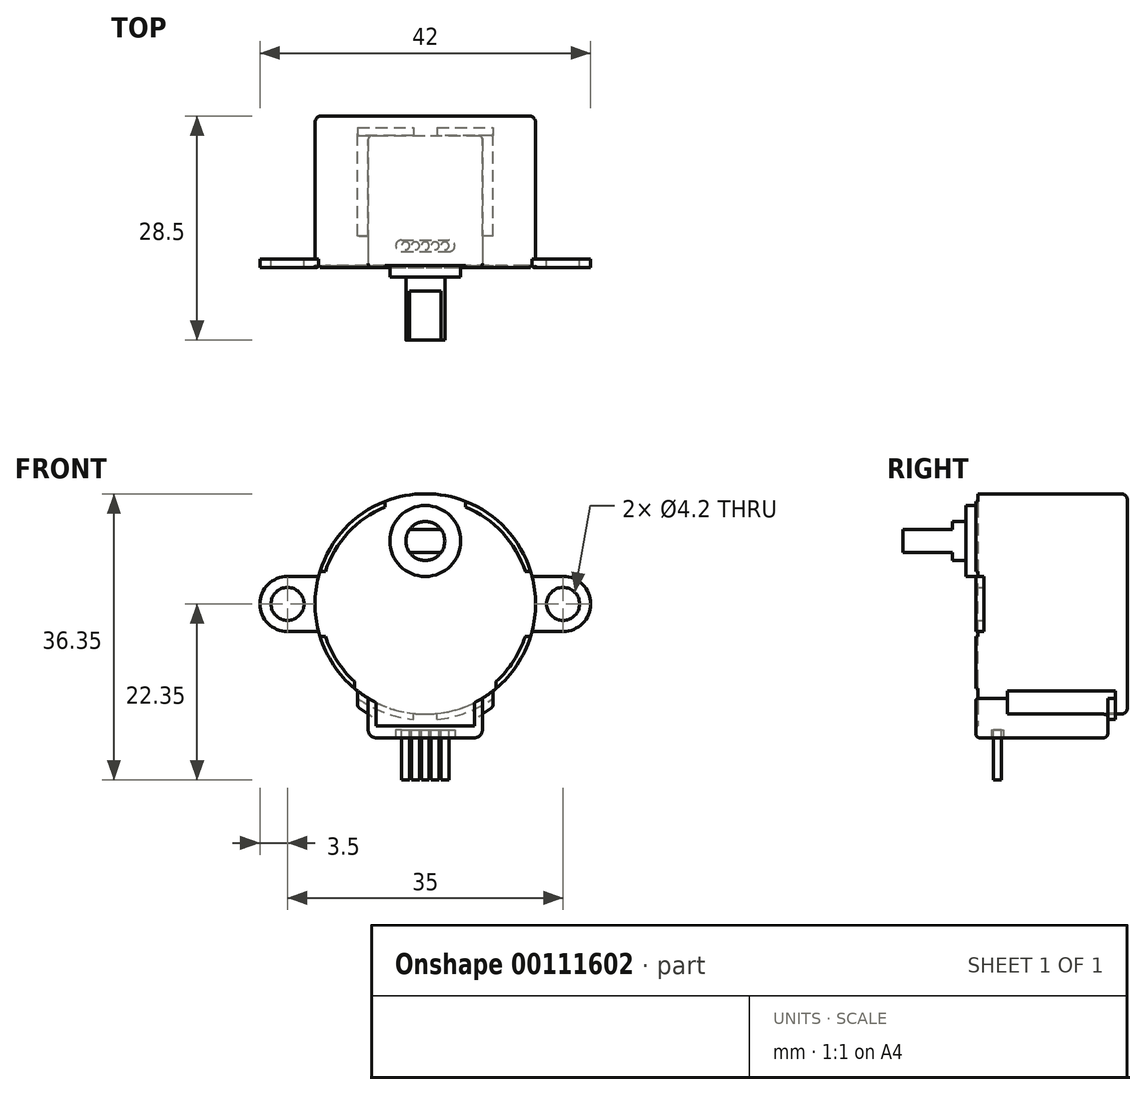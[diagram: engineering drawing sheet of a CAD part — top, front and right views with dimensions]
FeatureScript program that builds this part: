
annotation { "Feature Type Name" : "Feature", "Feature Type Description" : "" }
export const myFeature = defineFeature(function(context is Context, id is Id, definition is map)
    precondition{}
    {
        {
            var Q0;
            Q0=qCreatedBy(makeId("Front.planeOp"),FACE);
            var sketch = newSketch(context, id + "F0", { "sketchPlane" : qUnion([Q0])});
            skCircle(sketch, "E0", {"center": v(0, 0) * mm, "radius": 14 * mm});
            skSolve(sketch);
        }
        {
            var Q0;
            Q0=makeQuery(id+"F0.imprint","IMPRINT",FACE,{"disambiguationData":[TD([[makeQuery(id+"F0.imprint","IMPRINT",EDGE,{"derivedFrom":sQuery(id+"F0.wireOp",EDGE,"E0")}),1.0]])]});
            extrude(context, id + "F1", {"entities" : qUnion([Q0]), "depth" : 19 * mm});
        }
        {
            var Q0;
            Q0=makeQuery(id+"F1.opExtrude","CAP_EDGE",EDGE,{"disambiguationData":[OSD([sQuery(id+"F0.wireOp",EDGE,"E0")])],"isStart":true});
            fillet(context, id + "F2", {"entities" : qUnion([Q0]), "radius" : 0.8 * mm, "tangentPropagation" : true, "allowEdgeOverflow" : false});
        }
        {
            var Q0;
            Q0=makeQuery(id+"F1.opExtrude","CAP_FACE",FACE,{"disambiguationData":[OSD([sQuery(id+"F0.wireOp",EDGE,"E0")])],"isStart":false});
            var sketch = newSketch(context, id + "F3", { "sketchPlane" : qUnion([Q0])});
            skArc(sketch, "E1", {"start": v(12.7, 4.12) * mm, "mid": v(9.8, 9.06) * mm, "end": v(5.12, 12.33) * mm});
            skArc(sketch, "E2", {"start": v(-5.12, 12.33) * mm, "mid": v(-9.8, 9.06) * mm, "end": v(-12.7, 4.13) * mm});
            skLineSegment(sketch, "E3", {"start": v(-5.12, 12.33) * mm, "end": v(-5.12, 13.03) * mm});
            skLineSegment(sketch, "E4", {"start": v(-12.7, 4.12) * mm, "end": v(-13.38, 4.12) * mm});
            skLineSegment(sketch, "E5", {"start": v(12.7, 4.12) * mm, "end": v(13.38, 4.12) * mm});
            skLineSegment(sketch, "E6", {"start": v(5.12, 12.33) * mm, "end": v(5.12, 13.03) * mm});
            skArc(sketch, "E7", {"start": v(-12.7, -4.13) * mm, "mid": v(-11.22, -7.23) * mm, "end": v(-9, -9.86) * mm});
            skArc(sketch, "E8", {"start": v(9, -9.86) * mm, "mid": v(11.22, -7.23) * mm, "end": v(12.7, -4.12) * mm});
            skLineSegment(sketch, "E9", {"start": v(12.7, -4.12) * mm, "end": v(13.38, -4.12) * mm});
            skLineSegment(sketch, "E10", {"start": v(-12.7, -4.13) * mm, "end": v(-13.38, -4.13) * mm});
            skLineSegment(sketch, "E11", {"start": v(-9, -9.86) * mm, "end": v(-9, -10.72) * mm});
            skLineSegment(sketch, "E12", {"start": v(9, -9.86) * mm, "end": v(9, -10.72) * mm});
            skLineSegment(sketch, "E13", {"start": v(13.56, 3.5) * mm, "end": v(17.5, 3.5) * mm});
            skLineSegment(sketch, "E14", {"start": v(13.56, -3.5) * mm, "end": v(17.5, -3.5) * mm});
            skLineSegment(sketch, "E15", {"start": v(-13.56, 3.5) * mm, "end": v(-17.5, 3.5) * mm});
            skLineSegment(sketch, "E16", {"start": v(-13.56, -3.5) * mm, "end": v(-17.5, -3.5) * mm});
            skArc(sketch, "E17", {"start": v(17.5, -3.5) * mm, "mid": v(21, 0) * mm, "end": v(17.5, 3.5) * mm});
            skArc(sketch, "E18", {"start": v(-17.5, 3.5) * mm, "mid": v(-21, 0) * mm, "end": v(-17.5, -3.5) * mm});
            skCircle(sketch, "E19", {"center": v(-17.5, 0) * mm, "radius": 2.1 * mm});
            skCircle(sketch, "E20", {"center": v(17.5, 0) * mm, "radius": 2.1 * mm});
            skCircle(sketch, "E21", {"center": v(0, 8) * mm, "radius": 4.5 * mm});
            skSolve(sketch);
        }
        {
            var Q0;
            {var subQ1=sQuery(id+"F3.wireOp",EDGE,"E15");Q0=makeQuery(id+"F3.imprint","IMPRINT",FACE,{"disambiguationData":[TD([[makeQuery(id+"F3.imprint","IMPRINT",EDGE,{"derivedFrom":subQ1}),1.0]])]});}
            var Q1;
            {var subQ1=sQuery(id+"F3.wireOp",EDGE,"E13");Q1=makeQuery(id+"F3.imprint","IMPRINT",FACE,{"disambiguationData":[TD([[makeQuery(id+"F3.imprint","IMPRINT",EDGE,{"derivedFrom":subQ1}),-1.0]])]});}
            var Q2;
            Q2=makeQuery(id+"F3.imprint","IMPRINT",FACE,{"disambiguationData":[TD([[makeQuery(id+"F3.imprint","IMPRINT",EDGE,{"derivedFrom":sQuery(id+"F3.wireOp",EDGE,"E7")}),-1.0]])]});
            var Q3;
            Q3=makeQuery(id+"F3.imprint","IMPRINT",FACE,{"disambiguationData":[TD([[makeQuery(id+"F3.imprint","IMPRINT",EDGE,{"derivedFrom":sQuery(id+"F3.wireOp",EDGE,"E8")}),-1.0]])]});
            var Q4;
            Q4=makeQuery(id+"F3.imprint","IMPRINT",FACE,{"disambiguationData":[TD([[makeQuery(id+"F3.imprint","IMPRINT",EDGE,{"derivedFrom":sQuery(id+"F3.wireOp",EDGE,"E1")}),-1.0]])]});
            var Q5;
            Q5=makeQuery(id+"F3.imprint","IMPRINT",FACE,{"disambiguationData":[TD([[makeQuery(id+"F3.imprint","IMPRINT",EDGE,{"derivedFrom":sQuery(id+"F3.wireOp",EDGE,"E2")}),-1.0]])]});
            var Q6;
            Q6=makeQuery(id+"F3.imprint","IMPRINT",FACE,{"disambiguationData":[TD([[makeQuery(id+"F3.imprint","IMPRINT",EDGE,{"derivedFrom":sQuery(id+"F3.wireOp",EDGE,"E21")}),1.0]])]});
            extrude(context, id + "F4", {"entities" : qUnion([Q0, Q1, Q2, Q3, Q4, Q5, Q6]), "operationType" : NewBodyOperationType.ADD, "depth" : .25 * mm, "hasSecondDirection" : true, "secondDirectionOppositeDirection" : true, "secondDirectionDepth" : .8 * mm});
        }
        {
            var Q0;
            {var subQ0=sQuery(id+"F0.wireOp",EDGE,"E0");var subQ1=makeQuery(id+"F1.opExtrude","CAP_EDGE",EDGE,{"disambiguationData":[OSD([subQ0])],"isStart":false});Q0=makeQuery(id+"F4.opExtrude","CAP_EDGE",EDGE,{"disambiguationData":[OSD([subQ0]),TDD([makeQuery(id+"F3.imprint","IMPRINT",EDGE,{"disambiguationData":[TD([[makeQuery(id+"F3.imprint","INTERSECT",VERTEX,{"derivedFrom":[subQ1,sQuery(id+"F3.wireOp",EDGE,"E15")]}),-1.0]])],"derivedFrom":subQ1})])],"isStart":false});}
            var Q1;
            {var subQ0=sQuery(id+"F0.wireOp",EDGE,"E0");var subQ1=makeQuery(id+"F1.opExtrude","CAP_EDGE",EDGE,{"disambiguationData":[OSD([subQ0])],"isStart":false});Q1=makeQuery(id+"F4.opExtrude","CAP_EDGE",EDGE,{"disambiguationData":[OSD([subQ0]),TDD([makeQuery(id+"F3.imprint","IMPRINT",EDGE,{"disambiguationData":[TD([[makeQuery(id+"F3.imprint","INTERSECT",VERTEX,{"derivedFrom":[subQ1,sQuery(id+"F3.wireOp",EDGE,"E13")]}),1.0]])],"derivedFrom":subQ1})])],"isStart":false});}
            fillet(context, id + "F5", {"entities" : qUnion([Q0, Q1]), "radius" : 0.25 * mm, "tangentPropagation" : true, "allowEdgeOverflow" : false});
        }
        {
            var Q0;
            Q0=makeQuery(id+"F4.opExtrude","CAP_FACE",FACE,{"disambiguationData":[OSD([sQuery(id+"F3.wireOp",EDGE,"E21")])],"isStart":false});
            extrude(context, id + "F6", {"entities" : qUnion([Q0]), "operationType" : NewBodyOperationType.ADD, "depth" : 1.25 * mm});
        }
        {
            var Q0;
            Q0=makeQuery(id+"F1.opExtrude","CAP_FACE",FACE,{"disambiguationData":[OSD([sQuery(id+"F0.wireOp",EDGE,"E0")])],"isStart":false});
            var sketch = newSketch(context, id + "F7", { "sketchPlane" : qUnion([Q0])});
            skLineSegment(sketch, "E22", {"start": v(-7.25, -11.98) * mm, "end": v(-7.25, -16) * mm});
            skLineSegment(sketch, "E23", {"start": v(-6.25, -17) * mm, "end": v(6.25, -17) * mm});
            skLineSegment(sketch, "E24", {"start": v(7.25, -16) * mm, "end": v(7.25, -11.98) * mm});
            skPoint(sketch, "E25.visualSharp", {"position": v(-7.25, -17) * mm});
            skArc(sketch, "E25.filletArc", {"start": v(-7.25, -16) * mm, "mid": v(-6.96, -16.7) * mm, "end": v(-6.25, -17) * mm});
            skPoint(sketch, "E26.visualSharp", {"position": v(7.25, -17) * mm});
            skArc(sketch, "E26.filletArc", {"start": v(6.25, -17) * mm, "mid": v(6.96, -16.7) * mm, "end": v(7.25, -16) * mm});
            skLineSegment(sketch, "E27.0", {"start": v(-6.25, -15.5) * mm, "end": v(6.25, -15.5) * mm});
            skLineSegment(sketch, "E28.0", {"start": v(-6.25, -12.53) * mm, "end": v(-6.25, -15.5) * mm});
            skLineSegment(sketch, "E29.0", {"start": v(6.25, -15.5) * mm, "end": v(6.25, -12.53) * mm});
            skSolve(sketch);
        }
        {
            var Q0;
            Q0=makeQuery(id+"F7.imprint","IMPRINT",FACE,{"disambiguationData":[TD([[makeQuery(id+"F7.imprint","IMPRINT",EDGE,{"derivedFrom":sQuery(id+"F7.wireOp",EDGE,"E27.0")}),1.0]])]});
            var Q1;
            {var subQ2=sQuery(id+"F7.wireOp",EDGE,"E22");Q1=makeQuery(id+"F7.imprint","IMPRINT",FACE,{"disambiguationData":[TD([[makeQuery(id+"F7.imprint","IMPRINT",EDGE,{"derivedFrom":subQ2}),1.0]])]});}
            extrude(context, id + "F8", {"entities" : qUnion([Q0, Q1]), "operationType" : NewBodyOperationType.ADD, "oppositeDirection" : true, "depth" : 16.5 * mm});
        }
        {
            var Q0;
            {var subQ2=sQuery(id+"F7.wireOp",EDGE,"E22");Q0=makeQuery(id+"F7.imprint","IMPRINT",FACE,{"disambiguationData":[TD([[makeQuery(id+"F7.imprint","IMPRINT",EDGE,{"derivedFrom":subQ2}),1.0]])]});}
            extrude(context, id + "F9", {"entities" : qUnion([Q0]), "operationType" : NewBodyOperationType.ADD, "depth" : .25 * mm});
        }
        {
            var Q0;
            Q0=makeQuery(id+"F8.opExtrude","CAP_FACE",FACE,{"disambiguationData":[OSD([sQuery(id+"F0.wireOp",EDGE,"E0"),sQuery(id+"F7.wireOp",EDGE,"E22"),sQuery(id+"F7.wireOp",EDGE,"E23"),sQuery(id+"F7.wireOp",EDGE,"E24"),sQuery(id+"F7.wireOp",EDGE,"E25.filletArc"),sQuery(id+"F7.wireOp",EDGE,"E26.filletArc")])],"isStart":false});
            var sketch = newSketch(context, id + "F10", { "sketchPlane" : qUnion([Q0])});
            skCircle(sketch, "E30.0", {"center": v(0, 0) * mm, "radius": 14 * mm});
            skLineSegment(sketch, "E31", {"start": v(8.6, -11.05) * mm, "end": v(8.6, -13.05) * mm});
            skLineSegment(sketch, "E32", {"start": v(8.6, -13.05) * mm, "end": v(7.25, -14) * mm});
            skLineSegment(sketch, "E33", {"start": v(-8.6, -11.05) * mm, "end": v(-8.6, -13.05) * mm});
            skLineSegment(sketch, "E34", {"start": v(-8.6, -13.05) * mm, "end": v(-7.25, -14) * mm});
            skPoint(sketch, "E34.endSnap0", {"position": v(-7.25, -13.99) * mm});
            skArc(sketch, "E35", {"start": v(-8.6, -11.98) * mm, "mid": v(-5.23, -13.8) * mm, "end": v(-1.5, -14.67) * mm});
            skArc(sketch, "E36", {"start": v(1.5, -14.67) * mm, "mid": v(5.23, -13.8) * mm, "end": v(8.6, -11.98) * mm});
            skLineSegment(sketch, "E37", {"start": v(-1.5, -14.67) * mm, "end": v(-1.5, -13.92) * mm});
            skLineSegment(sketch, "E38", {"start": v(1.5, -14.67) * mm, "end": v(1.5, -13.92) * mm});
            skSolve(sketch);
        }
        {
            var Q0;
            {var subQ0=sQuery(id+"F10.wireOp",EDGE,"E34");Q0=makeQuery(id+"F10.imprint","IMPRINT",FACE,{"disambiguationData":[TD([[makeQuery(id+"F10.imprint","IMPRINT",EDGE,{"derivedFrom":subQ0}),1.0]])]});}
            var Q1;
            {var subQ0=sQuery(id+"F10.wireOp",EDGE,"E30.0");var subQ3=sQuery(id+"F10.wireOp",EDGE,"E33");var subQ4=makeQuery(id+"F10.imprint","INTERSECT",VERTEX,{"derivedFrom":[subQ0,subQ3]});Q1=makeQuery(id+"F10.imprint","IMPRINT",FACE,{"disambiguationData":[TD([[makeQuery(id+"F10.imprint","IMPRINT",EDGE,{"disambiguationData":[TD([[subQ4,-1.0]])],"derivedFrom":subQ0}),-1.0]])]});}
            var Q2;
            {var subQ0=sQuery(id+"F10.wireOp",EDGE,"E32");Q2=makeQuery(id+"F10.imprint","IMPRINT",FACE,{"disambiguationData":[TD([[makeQuery(id+"F10.imprint","IMPRINT",EDGE,{"derivedFrom":subQ0}),-1.0]])]});}
            var Q3;
            {var subQ0=sQuery(id+"F10.wireOp",EDGE,"E30.0");var subQ3=sQuery(id+"F10.wireOp",EDGE,"E31");var subQ4=makeQuery(id+"F10.imprint","INTERSECT",VERTEX,{"derivedFrom":[subQ0,subQ3]});Q3=makeQuery(id+"F10.imprint","IMPRINT",FACE,{"disambiguationData":[TD([[makeQuery(id+"F10.imprint","IMPRINT",EDGE,{"disambiguationData":[TD([[subQ4,1.0]])],"derivedFrom":subQ0}),-1.0]])]});}
            extrude(context, id + "F11", {"entities" : qUnion([Q0, Q1, Q2, Q3]), "operationType" : NewBodyOperationType.ADD, "oppositeDirection" : true, "depth" : 12.75 * mm});
        }
        {
            var Q0;
            {var subQ3=sQuery(id+"F10.wireOp",EDGE,"E37");Q0=makeQuery(id+"F10.imprint","IMPRINT",FACE,{"disambiguationData":[TD([[makeQuery(id+"F10.imprint","IMPRINT",EDGE,{"derivedFrom":subQ3}),1.0]])]});}
            var Q1;
            {var subQ0=sQuery(id+"F10.wireOp",EDGE,"E30.0");var subQ3=sQuery(id+"F10.wireOp",EDGE,"E33");var subQ4=makeQuery(id+"F10.imprint","INTERSECT",VERTEX,{"derivedFrom":[subQ0,subQ3]});Q1=makeQuery(id+"F10.imprint","IMPRINT",FACE,{"disambiguationData":[TD([[makeQuery(id+"F10.imprint","IMPRINT",EDGE,{"disambiguationData":[TD([[subQ4,-1.0]])],"derivedFrom":subQ0}),-1.0]])]});}
            var Q2;
            {var subQ3=sQuery(id+"F10.wireOp",EDGE,"E38");Q2=makeQuery(id+"F10.imprint","IMPRINT",FACE,{"disambiguationData":[TD([[makeQuery(id+"F10.imprint","IMPRINT",EDGE,{"derivedFrom":subQ3}),-1.0]])]});}
            var Q3;
            {var subQ0=sQuery(id+"F10.wireOp",EDGE,"E30.0");var subQ3=sQuery(id+"F10.wireOp",EDGE,"E31");var subQ4=makeQuery(id+"F10.imprint","INTERSECT",VERTEX,{"derivedFrom":[subQ0,subQ3]});Q3=makeQuery(id+"F10.imprint","IMPRINT",FACE,{"disambiguationData":[TD([[makeQuery(id+"F10.imprint","IMPRINT",EDGE,{"disambiguationData":[TD([[subQ4,1.0]])],"derivedFrom":subQ0}),-1.0]])]});}
            extrude(context, id + "F12", {"entities" : qUnion([Q0, Q1, Q2, Q3]), "operationType" : NewBodyOperationType.ADD, "depth" : 1 * mm});
        }
        {
            var Q0;
            Q0=makeQuery(id+"F11.opExtrude","SWEPT_EDGE",EDGE,{"disambiguationData":[OSD([sQuery(id+"F10.wireOp",EDGE,"E33"),sQuery(id+"F10.wireOp",EDGE,"E34")])]});
            var Q1;
            Q1=makeQuery(id+"F11.opExtrude","SWEPT_EDGE",EDGE,{"disambiguationData":[OSD([sQuery(id+"F10.wireOp",EDGE,"E31"),sQuery(id+"F10.wireOp",EDGE,"E32")])]});
            var Q2;
            Q2=makeQuery(id+"F8.opExtrude","CAP_EDGE",EDGE,{"disambiguationData":[OSD([sQuery(id+"F7.wireOp",EDGE,"E23")])],"isStart":false});
            var Q3;
            Q3=makeQuery(id+"F9.opExtrude","CAP_EDGE",EDGE,{"disambiguationData":[OSD([sQuery(id+"F7.wireOp",EDGE,"E23")])],"isStart":false});
            fillet(context, id + "F13", {"entities" : qUnion([Q0, Q1, Q2, Q3]), "radius" : .5 * mm, "tangentPropagation" : true, "allowEdgeOverflow" : false});
        }
        {
            var Q0;
            Q0=makeQuery(id+"F6.opExtrude","CAP_FACE",FACE,{"disambiguationData":[OSD([sQuery(id+"F3.wireOp",EDGE,"E21")])],"isStart":false});
            var sketch = newSketch(context, id + "F14", { "sketchPlane" : qUnion([Q0])});
            skCircle(sketch, "E39", {"center": v(0, 8) * mm, "radius": 2.48 * mm});
            skLineSegment(sketch, "E40", {"start": v(-1.99, 9.48) * mm, "end": v(1.99, 9.48) * mm});
            skLineSegment(sketch, "E41", {"start": v(-1.99, 6.53) * mm, "end": v(1.99, 6.53) * mm});
            skSolve(sketch);
        }
        {
            var Q0;
            Q0=makeQuery(id+"F14.imprint","IMPRINT",FACE,{"disambiguationData":[TD([[makeQuery(id+"F14.imprint","IMPRINT",EDGE,{"derivedFrom":sQuery(id+"F14.wireOp",EDGE,"E39")}),1.0]])]});
            var Q1;
            {var subQ0=sQuery(id+"F14.wireOp",EDGE,"E41");Q1=makeQuery(id+"F14.imprint","IMPRINT",FACE,{"disambiguationData":[TD([[makeQuery(id+"F14.imprint","IMPRINT",EDGE,{"derivedFrom":subQ0}),-1.0]])]});}
            var Q2;
            {var subQ0=sQuery(id+"F14.wireOp",EDGE,"E40");Q2=makeQuery(id+"F14.imprint","IMPRINT",FACE,{"disambiguationData":[TD([[makeQuery(id+"F14.imprint","IMPRINT",EDGE,{"derivedFrom":subQ0}),1.0]])]});}
            extrude(context, id + "F15", {"entities" : qUnion([Q0, Q1, Q2]), "operationType" : NewBodyOperationType.ADD, "depth" : 1.75 * mm});
        }
        {
            var Q0;
            {var subQ0=sQuery(id+"F14.wireOp",EDGE,"E40");Q0=makeQuery(id+"F14.imprint","IMPRINT",FACE,{"disambiguationData":[TD([[makeQuery(id+"F14.imprint","IMPRINT",EDGE,{"derivedFrom":subQ0}),-1.0]])]});}
            extrude(context, id + "F16", {"entities" : qUnion([Q0]), "operationType" : NewBodyOperationType.ADD, "depth" : 8 * mm});
        }
        {
            var Q0;
            {var subQ0=sQuery(id+"F7.wireOp",EDGE,"E23");Q0=makeQuery(id+"F9.boolean.opBoolean","MERGE",FACE,{"derivedFrom":[makeQuery(id+"F8.opExtrude","SWEPT_FACE",FACE,{"disambiguationData":[OSD([subQ0])]}),makeQuery(id+"F9.opExtrude","SWEPT_FACE",FACE,{"disambiguationData":[OSD([subQ0])]})]});}
            var sketch = newSketch(context, id + "F17", { "sketchPlane" : qUnion([Q0])});
            skLineSegment(sketch, "E42", {"start": v(-3, 15.75) * mm, "end": v(3, 15.75) * mm});
            skLineSegment(sketch, "E43", {"start": v(-3, 17.25) * mm, "end": v(3, 17.25) * mm});
            skArc(sketch, "E44", {"start": v(-3, 17.25) * mm, "mid": v(-3.75, 16.5) * mm, "end": v(-3, 15.75) * mm});
            skArc(sketch, "E45", {"start": v(3, 15.75) * mm, "mid": v(3.75, 16.5) * mm, "end": v(3, 17.25) * mm});
            skLineSegment(sketch, "E46", {"start": v(-3, 16.5) * mm, "end": v(3, 16.5) * mm, "construction": true});
            skPoint(sketch, "E47", {"position": v(0, 16.5) * mm});
            skSolve(sketch);
        }
        {
            var Q0;
            Q0=makeQuery(id+"F17.imprint","IMPRINT",FACE,{"disambiguationData":[TD([[makeQuery(id+"F17.imprint","IMPRINT",EDGE,{"derivedFrom":sQuery(id+"F17.wireOp",EDGE,"E42")}),1.0]])]});
            extrude(context, id + "F18", {"entities" : qUnion([Q0]), "operationType" : NewBodyOperationType.REMOVE, "oppositeDirection" : true, "depth" : 1 * mm});
        }
        {
            var Q0;
            Q0=makeQuery(id+"F18.boolean.opBoolean","COPY",FACE,{"derivedFrom":makeQuery(id+"F18.opExtrude","CAP_FACE",FACE,{"disambiguationData":[OSD([sQuery(id+"F17.wireOp",EDGE,"E42"),sQuery(id+"F17.wireOp",EDGE,"E43"),sQuery(id+"F17.wireOp",EDGE,"E44"),sQuery(id+"F17.wireOp",EDGE,"E45")])],"isStart":false})});
            var sketch = newSketch(context, id + "F19", { "sketchPlane" : qUnion([Q0])});
            skLineSegment(sketch, "E48", {"start": v(-3, 16.5) * mm, "end": v(3, 16.5) * mm, "construction": true});
            skCircle(sketch, "E49", {"center": v(-2.5, 16.5) * mm, "radius": 0.5 * mm});
            skCircle(sketch, "E50", {"center": v(2.5, 16.5) * mm, "radius": 0.5 * mm});
            skCircle(sketch, "E51", {"center": v(0, 16.5) * mm, "radius": 0.5 * mm});
            skLineSegment(sketch, "E52", {"start": v(-2.5, 16.5) * mm, "end": v(0, 16.5) * mm, "construction": true});
            skLineSegment(sketch, "E53", {"start": v(0, 16.5) * mm, "end": v(2.5, 16.5) * mm, "construction": true});
            skCircle(sketch, "E54", {"center": v(-1.25, 16.5) * mm, "radius": 0.5 * mm});
            skCircle(sketch, "E55", {"center": v(1.25, 16.5) * mm, "radius": 0.5 * mm});
            skSolve(sketch);
        }
        {
            var Q0;
            Q0=makeQuery(id+"F19.imprint","IMPRINT",FACE,{"disambiguationData":[TD([[makeQuery(id+"F19.imprint","IMPRINT",EDGE,{"derivedFrom":sQuery(id+"F19.wireOp",EDGE,"E49")}),1.0]])]});
            var Q1;
            Q1=makeQuery(id+"F19.imprint","IMPRINT",FACE,{"disambiguationData":[TD([[makeQuery(id+"F19.imprint","IMPRINT",EDGE,{"derivedFrom":sQuery(id+"F19.wireOp",EDGE,"E54")}),1.0]])]});
            var Q2;
            Q2=makeQuery(id+"F19.imprint","IMPRINT",FACE,{"disambiguationData":[TD([[makeQuery(id+"F19.imprint","IMPRINT",EDGE,{"derivedFrom":sQuery(id+"F19.wireOp",EDGE,"E51")}),1.0]])]});
            var Q3;
            Q3=makeQuery(id+"F19.imprint","IMPRINT",FACE,{"disambiguationData":[TD([[makeQuery(id+"F19.imprint","IMPRINT",EDGE,{"derivedFrom":sQuery(id+"F19.wireOp",EDGE,"E55")}),1.0]])]});
            var Q4;
            Q4=makeQuery(id+"F19.imprint","IMPRINT",FACE,{"disambiguationData":[TD([[makeQuery(id+"F19.imprint","IMPRINT",EDGE,{"derivedFrom":sQuery(id+"F19.wireOp",EDGE,"E50")}),1.0]])]});
            extrude(context, id + "F20", {"entities" : qUnion([Q0, Q1, Q2, Q3, Q4]), "operationType" : NewBodyOperationType.ADD, "depth" : 6.35 * mm});
        }
    });
